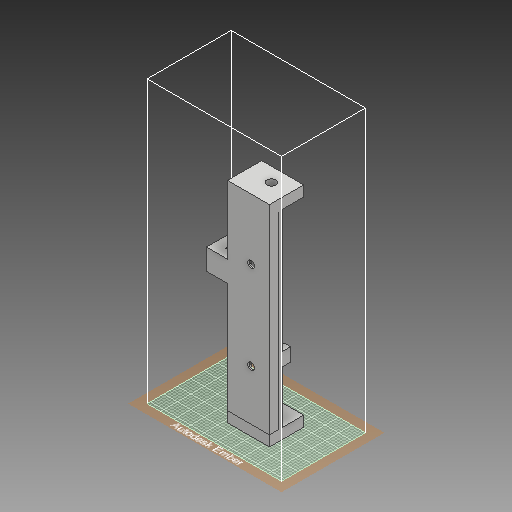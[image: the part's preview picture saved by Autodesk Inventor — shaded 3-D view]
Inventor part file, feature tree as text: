
AUTODESK INVENTOR PART (.ipt)
format: ipt  version: 2018 (Build 220112000, 112)  size: 632,832 bytes
history: native  units: mm
features: sketch x43, extrude x30, hole x8, fillet x5
ambient origin geometry x8: Origin, YZ Plane, XZ Plane, XY Plane, X Axis, Y Axis, Z Axis, Center Point
bodies: Solid1 (feature_tree)
feature tree (86):
  extrude  "Extrusion1"  Depth=100.0mm
  extrude  "Extrusion2"  Depth=5.0mm
  sketch  "Sketch3"  dims[d5=5.0mm d6=40.0mm d7=0.0mm]
  hole  "Hole1"  [1 undecoded]
  extrude  "Extrusion3"  Depth=2.0mm
  hole  "Hole2"  [1 undecoded]
  fillet  "Fillet1"  Radius=8.5mm
  extrude  "Extrusion4"  TaperAngle=90.0deg  [1 undecoded]
  extrude  "Extrusion5"  TaperAngle=180.0deg  [1 undecoded]
  hole  "Hole3"  [1 undecoded]
  fillet  "Fillet2"  Radius=3.5mm
  extrude  "Extrusion6"  Depth=10.0mm
  extrude  "Extrusion7"  Depth=5.0mm TaperAngle=0.0deg
  extrude  "Extrusion8"  Depth=5.0mm TaperAngle=0.0deg
  extrude  "Extrusion9"  Depth=0.1mm
  hole  "Hole4"  [1 undecoded]
  extrude  "Extrusion10"  Depth=5.5mm
  hole  "Hole5"  [1 undecoded]
  extrude  "Extrusion11"  Depth=2.1mm TaperAngle=0.0deg
  extrude  "Extrusion12"  Depth=5.0mm
  extrude  "Extrusion13"  Depth=1.0mm TaperAngle=0.0deg
  extrude  "Extrusion14"  Depth=3.8mm TaperAngle=0.0deg
  sketch  "Sketch21"  dims[d66=6.35mm d67=3.8mm d68=0.0mm]
  extrude  "Extrusion15"  Depth=8.0mm TaperAngle=0.0deg
  sketch  "Sketch23"  dims[d78=3.3mm d79=6.0mm d80=4.0mm d81=2.0mm d82=90.0deg d83=80.0mm d84=20.594885mm d85=5.45mm]
  extrude  "Extrusion16"  Depth=2.0mm
  extrude  "Extrusion17"  Depth=10.5mm
  hole  "Hole6"  [1 undecoded]
  fillet  "Fillet3"  Radius=4.5mm
  extrude  "Extrusion18"  Depth=8.0mm TaperAngle=0.0deg
  sketch  "Sketch28"  dims[d100=4.1mm d101=0.0mm d102=5.0mm]
  extrude  "Extrusion19"  Depth=10.0mm
  extrude  "Extrusion20"  Depth=5.0mm
  extrude  "Extrusion21"  Depth=10.0mm TaperAngle=0.0deg
  hole  "Hole7"  [1 undecoded]
  extrude  "Extrusion22"  Depth=21.0mm
  extrude  "Extrusion23"  Depth=7.499983mm TaperAngle=0.0deg
  fillet  "Fillet4"  Radius=50.0mm
  fillet  "Fillet5"  Radius=7.499983mm
  extrude  "Extrusion24"  Depth=10.0mm
  extrude  "Extrusion25"  Depth=4.1mm TaperAngle=0.0deg
  hole  "Hole8"  [1 undecoded]
  extrude  "Extrusion26"  Depth=8.0mm TaperAngle=0.0deg
  sketch  "Sketch39"  dims[d142=3.85mm d143=0.0mm d144=3.0mm]
  extrude  "Extrusion27"  Depth=1.0mm
  extrude  "Extrusion28"  Depth=3.0mm
  extrude  "Extrusion29"  Depth=100.0mm TaperAngle=0.0deg
  extrude  "Extrusion30"  Depth=10.0mm
  sketch  "Sketch1"  dims[d0=22.65mm d1=100.0mm]
  sketch  "Sketch2"  dims[d2=5.0mm d3=0.0mm d4=5.0mm]
  sketch  "Sketch4"  dims[d8=10.0mm]
  sketch  "Sketch5"  dims[d9=4.0mm d10=6.0mm d11=4.0mm d12=2.0mm d13=90.0deg d14=115.0mm d15=20.594885mm d16=23.0mm]
  sketch  "Sketch6"  dims[d17=102.75mm d18=0.0mm d19=1.175mm d20=8.5mm]
  sketch  "Sketch7"  dims[d21=21.0mm d22=90.0deg]
  sketch  "Sketch8"  dims[d23=8.5mm d24=180.0deg]
  sketch  "Sketch9"  dims[d25=21.0mm]
  sketch  "Sketch10"  dims[d26=4.0mm d27=6.0mm d28=4.0mm d29=2.0mm d30=90.0deg d31=115.0mm d32=20.594885mm d33=1.0mm d34=3.5mm]
  sketch  "Sketch11"  dims[d35=15.825mm d36=10.0mm]
  sketch  "Sketch12"  dims[d37=10.0mm d38=5.0mm d39=0.0mm]
  sketch  "Sketch13"  dims[d40=5.0mm d41=12.5mm d42=0.0mm]
  sketch  "Sketch14"  dims[d43=6.0mm d44=6.0mm d45=4.0mm d46=2.0mm d47=90.0deg d48=115.0mm d49=20.594885mm d50=0.1mm]
  sketch  "Sketch15"  dims[d51=4.25mm d52=1000.0mm d53=0.0mm]
  sketch  "Sketch16"  dims[d54=3.3mm d55=5.5mm]
  sketch  "Sketch17"  dims[d56=3.2mm d57=3.0mm]
  sketch  "Sketch18"  dims[d58=2.1mm d59=91.25mm d60=0.0mm]
  sketch  "Sketch19"  dims[d61=4.44mm d62=5.0mm]
  sketch  "Sketch20"  dims[d63=1.0mm d64=91.25mm d65=0.0mm]
  sketch  "Sketch22"  dims[d69=3.3mm d70=6.0mm d71=4.0mm d72=2.0mm d73=90.0deg d74=8.0mm d75=20.594885mm d76=4.55mm d77=0.0mm]
  sketch  "Sketch24"  dims[d86=129.8mm d87=0.0mm d88=10.5mm]
  sketch  "Sketch25"  dims[d89=2.5mm d90=0.0mm d91=10.0mm d92=4.5mm d93=0.0mm]
  sketch  "Sketch26"  dims[d94=8.0mm d95=0.0mm d96=15.5mm d97=0.0mm]
  sketch  "Sketch27"  dims[d98=10.0mm d99=10.0mm]
  sketch  "Sketch29"  dims[d103=17.5mm d104=10.0mm d105=0.0mm]
  sketch  "Sketch30"  dims[d106=5.0mm]
  sketch  "Sketch31"  dims[d107=6.0mm d108=6.0mm d109=4.0mm d110=2.0mm d111=90.0deg d112=80.0mm d113=20.594885mm d114=2.0mm]
  sketch  "Sketch32"  dims[d115=45.0mm d116=0.0mm d117=21.0mm]
  sketch  "Sketch33"  dims[d118=4.5mm d119=118.0mm d120=0.0mm d121=50.0mm d122=7.499983mm]
  sketch  "Sketch34"  dims[d123=7.5mm d124=10.0mm]
  sketch  "Sketch35"  dims[d125=10.0mm d126=4.1mm d127=0.0mm]
  sketch  "Sketch36"  dims[d128=13.4mm d129=0.0mm d130=5.0mm]
  sketch  "Sketch37"  dims[d131=6.0mm d132=6.0mm d133=4.0mm d134=2.0mm d135=90.0deg d136=8.0mm d137=20.594885mm d138=130.4mm d139=0.0mm]
  sketch  "Sketch38"  dims[d140=1.0mm d141=1.0mm]
  sketch  "Sketch40"  dims[d145=2.0mm d146=100.0mm d147=0.0mm]
  sketch  "Sketch41"  dims[d148=4.0mm d149=10.0mm]
  sketch  "Sketch42"  dims[d150=5.0mm]
  sketch  "Sketch43"  dims[d151=15.0mm d152=7.5mm d153=7.5mm d154=0.0mm d155=6.0mm d156=6.0mm d157=4.0mm d158=2.0mm d159=90.0deg d160=8.0mm d161=20.594885mm d162=5.5mm d163=5.0mm d164=0.0mm d165=5.5mm d166=0.0mm d167=2.0mm d168=0.0mm d169=2.0mm d170=0.0mm d171=2.0mm d172=0.0mm]
note: 10 required parameter values undecoded (feature->parameter linkage not recoverable at this tier; creation-order binding heuristic only, values carry confidence <= 0.55)
